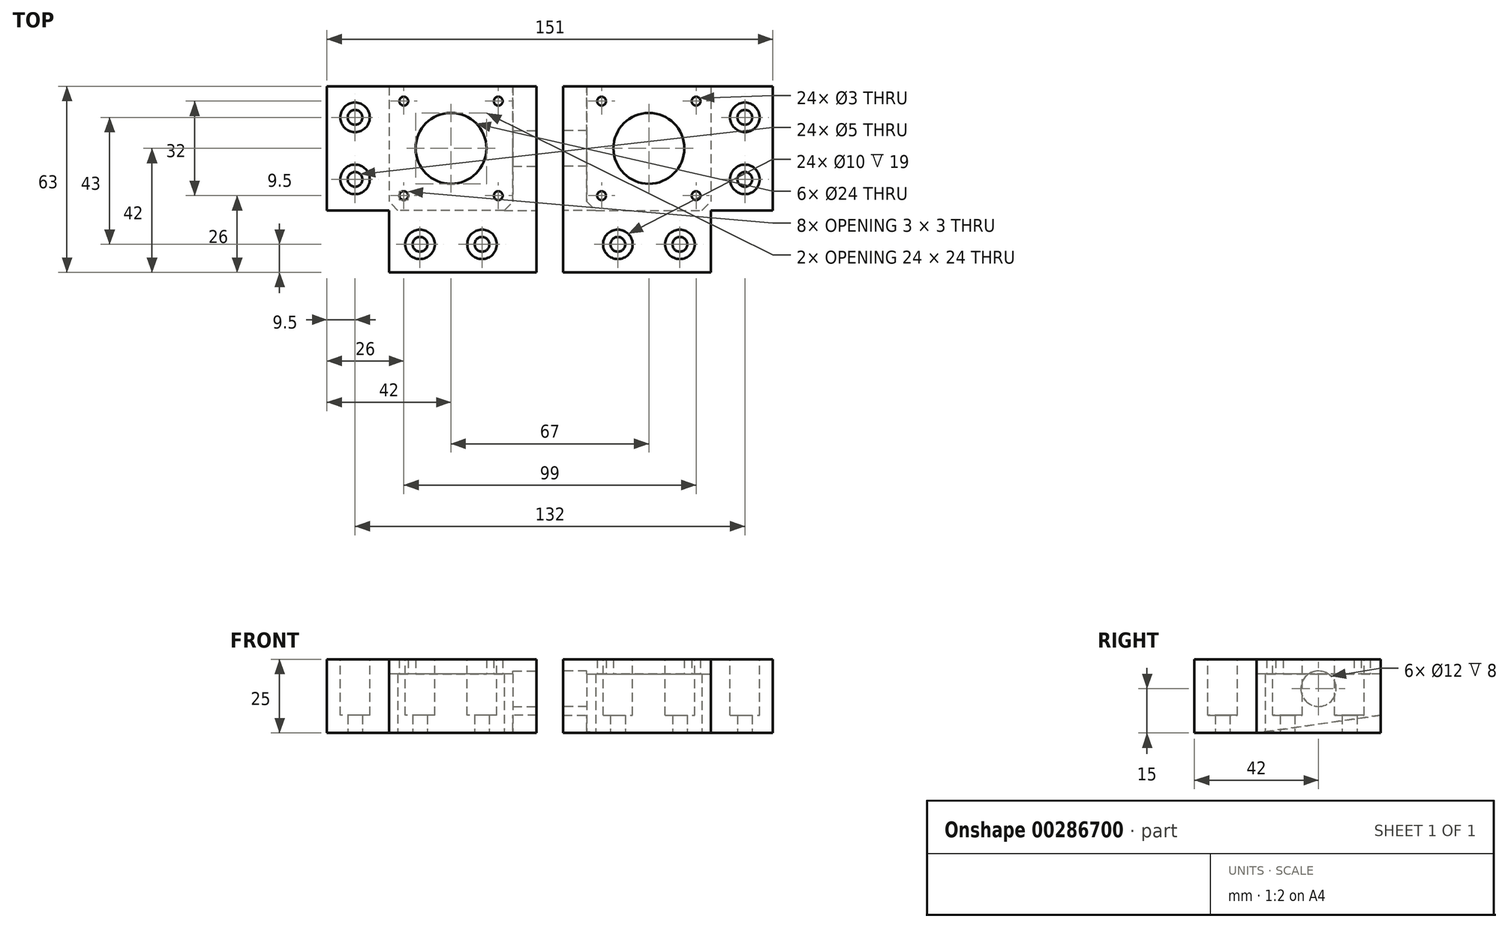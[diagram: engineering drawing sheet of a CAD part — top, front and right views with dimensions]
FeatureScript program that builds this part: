
annotation { "Feature Type Name" : "Feature", "Feature Type Description" : "" }
export const myFeature = defineFeature(function(context is Context, id is Id, definition is map)
    precondition{}
    {
        {
            var Q0;
            Q0=qCreatedBy(makeId("Top.planeOp"),FACE);
            var sketch = newSketch(context, id + "F0", { "sketchPlane" : qUnion([Q0])});
            skLineSegment(sketch, "E0.bottom", {"start": v(35.5, 31.5) * mm, "end": v(-35.5, 31.5) * mm});
            skLineSegment(sketch, "E0.top", {"start": v(35.5, -31.5) * mm, "end": v(-35.5, -31.5) * mm});
            skLineSegment(sketch, "E0.left", {"start": v(35.5, 31.5) * mm, "end": v(35.5, -31.5) * mm});
            skLineSegment(sketch, "E0.right", {"start": v(-35.5, 31.5) * mm, "end": v(-35.5, -31.5) * mm});
            skPoint(sketch, "E0.middle", {"position": v(0, 0) * mm});
            skSolve(sketch);
        }
        {
            var Q0;
            Q0 = qSketchRegion(id + "F0", true);
            extrude(context, id + "F1", {"entities" : qUnion([Q0]), "depth" : 25 * mm});
        }
        {
            var Q0;
            Q0=makeQuery(id+"F1.opExtrude","CAP_FACE",FACE,{"disambiguationData":[OSD([sQuery(id+"F0.wireOp",EDGE,"E0.bottom"),sQuery(id+"F0.wireOp",EDGE,"E0.top"),sQuery(id+"F0.wireOp",EDGE,"E0.left"),sQuery(id+"F0.wireOp",EDGE,"E0.right")])],"isStart":false});
            var sketch = newSketch(context, id + "F2", { "sketchPlane" : qUnion([Q0])});
            skLineSegment(sketch, "E1.bottom", {"start": v(-35.5, -31.5) * mm, "end": v(-14.5, -31.5) * mm});
            skLineSegment(sketch, "E1.top", {"start": v(-35.5, -10.5) * mm, "end": v(-14.5, -10.5) * mm});
            skLineSegment(sketch, "E1.left", {"start": v(-35.5, -31.5) * mm, "end": v(-35.5, -10.5) * mm});
            skLineSegment(sketch, "E1.right", {"start": v(-14.5, -31.5) * mm, "end": v(-14.5, -10.5) * mm});
            skSolve(sketch);
        }
        {
            var Q0;
            Q0 = qSketchRegion(id + "F2", true);
            extrude(context, id + "F3", {"entities" : qUnion([Q0]), "operationType" : NewBodyOperationType.REMOVE, "endBound" : BoundingType.THROUGH_ALL, "oppositeDirection" : true, "depth" : 25 * mm});
        }
        {
            var Q0;
            Q0=qCreatedBy(makeId("Top.planeOp"),FACE);
            var sketch = newSketch(context, id + "F4", { "sketchPlane" : qUnion([Q0])});
            skCircle(sketch, "E2", {"center": v(6.5, 10.5) * mm, "radius": 12 * mm});
            skSolve(sketch);
        }
        {
            var Q0;
            Q0 = qSketchRegion(id + "F4", true);
            extrude(context, id + "F5", {"entities" : qUnion([Q0]), "operationType" : NewBodyOperationType.REMOVE, "endBound" : BoundingType.THROUGH_ALL, "depth" : 25 * mm});
        }
        {
            var Q0;
            Q0=qCreatedBy(makeId("Top.planeOp"),FACE);
            var sketch = newSketch(context, id + "F6", { "sketchPlane" : qUnion([Q0])});
            skCircle(sketch, "E3", {"center": v(22.5, 26.5) * mm, "radius": 1.5 * mm});
            skLineSegment(sketch, "E4.bottom", {"start": v(22.5, 26.5) * mm, "end": v(-9.5, 26.5) * mm, "construction": true});
            skLineSegment(sketch, "E4.top", {"start": v(22.5, -5.5) * mm, "end": v(-9.5, -5.5) * mm, "construction": true});
            skLineSegment(sketch, "E4.left", {"start": v(22.5, 26.5) * mm, "end": v(22.5, -5.5) * mm, "construction": true});
            skLineSegment(sketch, "E4.right", {"start": v(-9.5, 26.5) * mm, "end": v(-9.5, -5.5) * mm, "construction": true});
            skPoint(sketch, "E4.middle", {"position": v(6.5, 10.5) * mm});
            skCircle(sketch, "E5", {"center": v(22.5, -5.5) * mm, "radius": 1.5 * mm});
            skCircle(sketch, "E6", {"center": v(-9.5, -5.5) * mm, "radius": 1.5 * mm});
            skCircle(sketch, "E7", {"center": v(-9.5, 26.5) * mm, "radius": 1.5 * mm});
            skSolve(sketch);
        }
        {
            var Q0;
            Q0 = qSketchRegion(id + "F6", true);
            extrude(context, id + "F7", {"entities" : qUnion([Q0]), "operationType" : NewBodyOperationType.REMOVE, "endBound" : BoundingType.THROUGH_ALL, "depth" : 25 * mm});
        }
        {
            var Q0;
            Q0=qCreatedBy(makeId("Top.planeOp"),FACE);
            var sketch = newSketch(context, id + "F8", { "sketchPlane" : qUnion([Q0])});
            skCircle(sketch, "E8", {"center": v(-26, 21) * mm, "radius": 2.5 * mm});
            skCircle(sketch, "E9", {"center": v(-26, 0) * mm, "radius": 2.5 * mm});
            skCircle(sketch, "E10", {"center": v(-4, -22) * mm, "radius": 2.5 * mm});
            skCircle(sketch, "E11", {"center": v(17, -22) * mm, "radius": 2.5 * mm});
            skSolve(sketch);
        }
        {
            var Q0;
            Q0 = qSketchRegion(id + "F8", true);
            extrude(context, id + "F9", {"entities" : qUnion([Q0]), "operationType" : NewBodyOperationType.REMOVE, "endBound" : BoundingType.THROUGH_ALL, "depth" : 25 * mm});
        }
        {
            var Q0;
            Q0=makeQuery(id+"F1.opExtrude","CAP_FACE",FACE,{"disambiguationData":[OSD([sQuery(id+"F0.wireOp",EDGE,"E0.bottom"),sQuery(id+"F0.wireOp",EDGE,"E0.top"),sQuery(id+"F0.wireOp",EDGE,"E0.left"),sQuery(id+"F0.wireOp",EDGE,"E0.right")])],"isStart":false});
            var sketch = newSketch(context, id + "F10", { "sketchPlane" : qUnion([Q0])});
            skCircle(sketch, "E12", {"center": v(17, -22) * mm, "radius": 5 * mm});
            skCircle(sketch, "E13", {"center": v(-4, -22) * mm, "radius": 5 * mm});
            skCircle(sketch, "E14", {"center": v(-26, 0) * mm, "radius": 5 * mm});
            skCircle(sketch, "E15", {"center": v(-26, 21) * mm, "radius": 5 * mm});
            skSolve(sketch);
        }
        {
            var Q0;
            Q0 = qSketchRegion(id + "F10", true);
            extrude(context, id + "F11", {"entities" : qUnion([Q0]), "operationType" : NewBodyOperationType.REMOVE, "oppositeDirection" : true, "depth" : 19 * mm});
        }
        {
            var Q0;
            Q0=makeQuery(id+"F1.opExtrude","CAP_FACE",FACE,{"disambiguationData":[OSD([sQuery(id+"F0.wireOp",EDGE,"E0.bottom"),sQuery(id+"F0.wireOp",EDGE,"E0.top"),sQuery(id+"F0.wireOp",EDGE,"E0.left"),sQuery(id+"F0.wireOp",EDGE,"E0.right")])],"isStart":true});
            var sketch = newSketch(context, id + "F12", { "sketchPlane" : qUnion([Q0])});
            skLineSegment(sketch, "E16.bottom", {"start": v(27.5, -31.5) * mm, "end": v(-14.5, -31.5) * mm});
            skLineSegment(sketch, "E16.top", {"start": v(24.5, 10.5) * mm, "end": v(-11.5, 10.5) * mm});
            skLineSegment(sketch, "E16.left", {"start": v(27.5, -31.5) * mm, "end": v(27.5, 7.5) * mm});
            skLineSegment(sketch, "E16.right", {"start": v(-14.5, -31.5) * mm, "end": v(-14.5, 7.5) * mm});
            skPoint(sketch, "E16.middle", {"position": v(6.5, -10.5) * mm});
            skLineSegment(sketch, "E17", {"start": v(-11.5, 10.5) * mm, "end": v(-14.5, 7.5) * mm});
            skPoint(sketch, "E18.orphan", {"position": v(-14.5, 10.5) * mm});
            skLineSegment(sketch, "E19", {"start": v(27.5, 7.5) * mm, "end": v(24.5, 10.5) * mm});
            skPoint(sketch, "E20.orphan", {"position": v(27.5, 10.5) * mm});
            skSolve(sketch);
        }
        {
            var Q0;
            Q0 = qSketchRegion(id + "F12", true);
            extrude(context, id + "F13", {"entities" : qUnion([Q0]), "operationType" : NewBodyOperationType.REMOVE, "oppositeDirection" : true, "depth" : 20 * mm});
        }
        {
            var Q0;
            Q0=makeQuery(id+"F1.opExtrude","SWEPT_FACE",FACE,{"disambiguationData":[OSD([sQuery(id+"F0.wireOp",EDGE,"E0.left")])]});
            var sketch = newSketch(context, id + "F14", { "sketchPlane" : qUnion([Q0])});
            skCircle(sketch, "E21", {"center": v(10.5, 15) * mm, "radius": 6 * mm});
            skSolve(sketch);
        }
        {
            var Q0;
            Q0 = qSketchRegion(id + "F14", true);
            var Q1;
            Q1=makeQuery(id+"F13.boolean.opBoolean","COPY",FACE,{"derivedFrom":makeQuery(id+"F13.opExtrude","SWEPT_FACE",FACE,{"disambiguationData":[OSD([sQuery(id+"F12.wireOp",EDGE,"E16.left")])]})});
            extrude(context, id + "F15", {"entities" : qUnion([Q0]), "operationType" : NewBodyOperationType.REMOVE, "endBound" : BoundingType.UP_TO_SURFACE, "oppositeDirection" : true, "endBoundEntityFace" : qUnion([Q1]), "depth" : 25 * mm});
        }
        {
            var Q0;
            {var subQ0=sQuery(id+"F0.wireOp",EDGE,"E0.bottom");var subQ1=sQuery(id+"F0.wireOp",EDGE,"E0.left");Q0=makeQuery(id+"F13.boolean.opBoolean","SPLIT",EDGE,{"disambiguationData":[TD([makeQuery(id+"F1.opExtrude","SWEPT_FACE",FACE,{"disambiguationData":[OSD([subQ1])]})])],"derivedFrom":makeQuery(id+"F1.opExtrude","CAP_EDGE",EDGE,{"disambiguationData":[OSD([subQ0])],"isStart":true})});}
            chamfer(context, id + "F16", {"entities" : qUnion([Q0]), "chamferType" : ChamferType.TWO_OFFSETS, "width1" : 6 * mm, "oppositeDirection" : false, "width2" : 42 * mm, "tangentPropagation" : true});
        }
        {
            var Q0;
            Q0=qCreatedBy(makeId("Right.planeOp"),FACE);
            cPlane(context, id + "F17", {"entities" : qUnion([Q0]), "cplaneType" : CPlaneType.OFFSET, "offset" : 40 * mm, "width" : 150 * mm, "height" : 150 * mm});
        }
        {
            var Q0;
            Q0=makeQuery(id+"F1.opExtrude","SWEPT_BODY",BODY,{"disambiguationData":[OSD([sQuery(id+"F0.wireOp",EDGE,"E0.bottom"),sQuery(id+"F0.wireOp",EDGE,"E0.top"),sQuery(id+"F0.wireOp",EDGE,"E0.left"),sQuery(id+"F0.wireOp",EDGE,"E0.right")])]});
            var Q1;
            Q1=qCreatedBy(id+"F17.planeOp",FACE);
            mirror(context, id + "F18", {"entities" : qUnion([Q0]), "mirrorPlane" : qUnion([Q1])});
        }
    });
